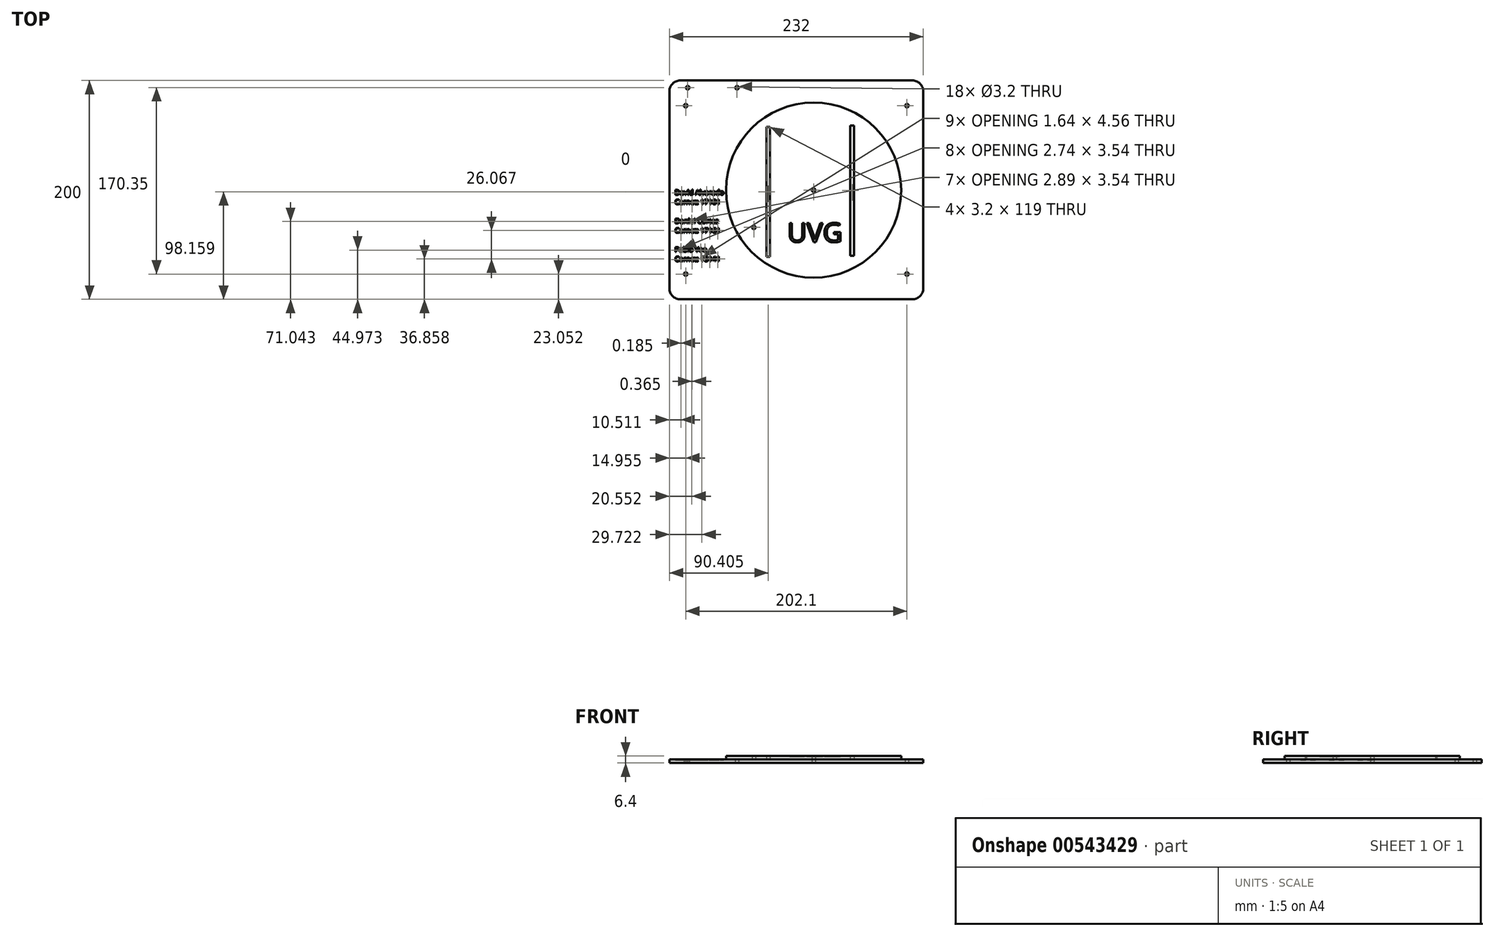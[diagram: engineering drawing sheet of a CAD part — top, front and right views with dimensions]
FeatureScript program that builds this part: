
annotation { "Feature Type Name" : "Feature", "Feature Type Description" : "" }
export const myFeature = defineFeature(function(context is Context, id is Id, definition is map)
    precondition{}
    {
        {
            var Q0;
            Q0=qCreatedBy(makeId("Top.planeOp"),FACE);
            var sketch = newSketch(context, id + "F0", { "sketchPlane" : qUnion([Q0])});
            skLineSegment(sketch, "E0.bottom", {"start": v(-92.28, 107.73) * mm, "end": v(139.72, 107.73) * mm});
            skLineSegment(sketch, "E0.top", {"start": v(-92.28, -92.27) * mm, "end": v(139.72, -92.27) * mm});
            skLineSegment(sketch, "E0.left", {"start": v(-92.28, 107.73) * mm, "end": v(-92.28, -92.27) * mm});
            skLineSegment(sketch, "E0.right", {"start": v(139.72, 107.73) * mm, "end": v(139.72, -92.27) * mm});
            skCircle(sketch, "E1", {"center": v(39.52, 7.53) * mm, "radius": 1.6 * mm});
            skCircle(sketch, "E2", {"center": v(-75.5, 101.13) * mm, "radius": 1.6 * mm});
            skCircle(sketch, "E3", {"center": v(-30.4, 101.13) * mm, "radius": 1.6 * mm});
            skCircle(sketch, "E4", {"center": v(-77.33, 84.68) * mm, "radius": 1.6 * mm});
            skCircle(sketch, "E5", {"center": v(124.77, 84.68) * mm, "radius": 1.6 * mm});
            skCircle(sketch, "E6", {"center": v(124.77, -69.22) * mm, "radius": 1.6 * mm});
            skCircle(sketch, "E7", {"center": v(-77.33, -69.22) * mm, "radius": 1.6 * mm});
            skSolve(sketch);
        }
        {
            var Q0;
            Q0=makeQuery(id+"F0.imprint","IMPRINT",FACE,{"disambiguationData":[TD([[makeQuery(id+"F0.imprint","IMPRINT",EDGE,{"derivedFrom":sQuery(id+"F0.wireOp",EDGE,"E0.bottom")}),-1.0]])]});
            extrude(context, id + "F1", {"entities" : qUnion([Q0]), "depth" : 3.2 * mm});
        }
        {
            var Q0;
            Q0=makeQuery(id+"F1.opExtrude","SWEPT_EDGE",EDGE,{"disambiguationData":[OSD([sQuery(id+"F0.wireOp",EDGE,"E0.bottom"),sQuery(id+"F0.wireOp",EDGE,"E0.right")])]});
            var Q1;
            Q1=makeQuery(id+"F1.opExtrude","SWEPT_EDGE",EDGE,{"disambiguationData":[OSD([sQuery(id+"F0.wireOp",EDGE,"E0.bottom"),sQuery(id+"F0.wireOp",EDGE,"E0.left")])]});
            var Q2;
            Q2=makeQuery(id+"F1.opExtrude","SWEPT_EDGE",EDGE,{"disambiguationData":[OSD([sQuery(id+"F0.wireOp",EDGE,"E0.top"),sQuery(id+"F0.wireOp",EDGE,"E0.right")])]});
            var Q3;
            Q3=makeQuery(id+"F1.opExtrude","SWEPT_EDGE",EDGE,{"disambiguationData":[OSD([sQuery(id+"F0.wireOp",EDGE,"E0.top"),sQuery(id+"F0.wireOp",EDGE,"E0.left")])]});
            fillet(context, id + "F2", {"entities" : qUnion([Q0, Q1, Q2, Q3]), "radius" : 10 * mm, "tangentPropagation" : true, "allowEdgeOverflow" : false});
        }
        {
            var Q0;
            Q0=makeQuery(id+"F1.opExtrude","CAP_FACE",FACE,{"disambiguationData":[OSD([sQuery(id+"F0.wireOp",EDGE,"E0.bottom"),sQuery(id+"F0.wireOp",EDGE,"E0.top"),sQuery(id+"F0.wireOp",EDGE,"E0.left"),sQuery(id+"F0.wireOp",EDGE,"E0.right"),sQuery(id+"F0.wireOp",EDGE,"E1")])],"isStart":false});
            var sketch = newSketch(context, id + "F3", { "sketchPlane" : qUnion([Q0])});
            skCircle(sketch, "E8", {"center": v(39.52, 7.53) * mm, "radius": 80 * mm});
            skCircle(sketch, "E9", {"center": v(39.52, 7.53) * mm, "radius": 1.6 * mm});
            skLineSegment(sketch, "E10.bottom", {"start": v(76.32, 66.6) * mm, "end": v(73.12, 66.6) * mm});
            skLineSegment(sketch, "E10.top", {"start": v(76.32, -52.4) * mm, "end": v(73.12, -52.4) * mm});
            skLineSegment(sketch, "E10.left", {"start": v(76.32, 66.6) * mm, "end": v(76.32, -52.4) * mm});
            skLineSegment(sketch, "E10.right", {"start": v(73.12, 66.6) * mm, "end": v(73.12, -52.4) * mm});
            skLineSegment(sketch, "E11.bottom", {"start": v(-3.48, 65.39) * mm, "end": v(-0.28, 65.39) * mm});
            skLineSegment(sketch, "E11.top", {"start": v(-3.48, -53.61) * mm, "end": v(-0.28, -53.61) * mm});
            skLineSegment(sketch, "E11.left", {"start": v(-3.48, 65.39) * mm, "end": v(-3.48, -53.61) * mm});
            skLineSegment(sketch, "E11.right", {"start": v(-0.28, 65.39) * mm, "end": v(-0.28, -53.61) * mm});
            skCircle(sketch, "E12", {"center": v(-15.08, -26.62) * mm, "radius": 1.6 * mm});
            skSolve(sketch);
        }
        {
            var Q0;
            Q0=makeQuery(id+"F3.imprint","IMPRINT",FACE,{"disambiguationData":[TD([[makeQuery(id+"F3.imprint","IMPRINT",EDGE,{"derivedFrom":sQuery(id+"F3.wireOp",EDGE,"E8")}),1.0]])]});
            var Q1;
            Q1=makeQuery(id+"F1.opExtrude","CAP_FACE",FACE,{"disambiguationData":[OSD([sQuery(id+"F0.wireOp",EDGE,"E0.bottom"),sQuery(id+"F0.wireOp",EDGE,"E0.top"),sQuery(id+"F0.wireOp",EDGE,"E0.left"),sQuery(id+"F0.wireOp",EDGE,"E0.right"),sQuery(id+"F0.wireOp",EDGE,"E1")])],"isStart":true});
            extrude(context, id + "F4", {"entities" : qUnion([Q0, Q1]), "depth" : 3.2 * mm, "offsetDistance" : 25 * mm});
        }
        {
            var Q0;
            Q0=qSketchRegion(id+"F3",true);
            extrude(context, id + "F5", {"entities" : qUnion([Q0]), "depth" : 3.2 * mm, "offsetDistance" : 25 * mm});
        }
        {
            var Q0;
            {var subQ0=sQuery(id+"F0.wireOp",EDGE,"E0.right");var subQ1=sQuery(id+"F0.wireOp",EDGE,"E3");var subQ2=sQuery(id+"F0.wireOp",EDGE,"E2");var subQ3=sQuery(id+"F0.wireOp",EDGE,"E1");var subQ4=sQuery(id+"F0.wireOp",EDGE,"E0.left");var subQ5=sQuery(id+"F0.wireOp",EDGE,"E0.top");var subQ6=sQuery(id+"F0.wireOp",EDGE,"E0.bottom");Q0=makeQuery(id+"FOxecQIyzaDJO3S_3.boolean.opBoolean","SPLIT",FACE,{"disambiguationData":[TD([makeQuery(id+"F1.opExtrude","SWEPT_FACE",FACE,{"disambiguationData":[OSD([subQ6])]})])],"derivedFrom":makeQuery(id+"F1.opExtrude","CAP_FACE",FACE,{"disambiguationData":[OSD([subQ6,subQ5,subQ4,subQ0,subQ3,subQ2,subQ1])],"isStart":false})});}
            var sketch = newSketch(context, id + "F6", { "sketchPlane" : qUnion([Q0])});
            skText(sketch, "E13", { "text": "David Alvarado\nCarnet: 17101\n\nDaniel Cortez\nCarnet: 17161\n\nPablo Yee\nCarnet: 15141", "fontName": "OpenSans-Regular.ttf"});
            const initialGuessF6  = {"E13": [-0.08728, 0.00313, 1, 0, 0.0046]};
            skSetInitialGuess(sketch, initialGuessF6);
            skSolve(sketch);
        }
        {
            var Q0;
            Q0 = qSketchRegion(id + "F6", true);
            extrude(context, id + "F7", {"entities" : qUnion([Q0]), "operationType" : NewBodyOperationType.REMOVE, "oppositeDirection" : true, "depth" : 0.5 * mm, "offsetDistance" : 25 * mm});
        }
        {
            var Q0;
            Q0=makeQuery(id+"F4.opExtrude","CAP_FACE",FACE,{"disambiguationData":[OSD([sQuery(id+"F3.wireOp",EDGE,"E8"),sQuery(id+"F3.wireOp",EDGE,"E9"),sQuery(id+"F3.wireOp",EDGE,"E10.bottom"),sQuery(id+"F3.wireOp",EDGE,"E10.top"),sQuery(id+"F3.wireOp",EDGE,"E10.left"),sQuery(id+"F3.wireOp",EDGE,"E10.right"),sQuery(id+"F3.wireOp",EDGE,"E11.bottom"),sQuery(id+"F3.wireOp",EDGE,"E11.top"),sQuery(id+"F3.wireOp",EDGE,"E11.left"),sQuery(id+"F3.wireOp",EDGE,"E11.right"),sQuery(id+"F3.wireOp",EDGE,"E12")])],"isStart":false});
            var sketch = newSketch(context, id + "F8", { "sketchPlane" : qUnion([Q0])});
            skText(sketch, "E14", { "text": "UVG", "fontName": "OpenSans-Regular.ttf"});
            const initialGuessF8  = {"E14": [0.01552, -0.04002, 1, 0, 0.01762]};
            skSetInitialGuess(sketch, initialGuessF8);
            skSolve(sketch);
        }
        {
            var Q0;
            Q0 = qSketchRegion(id + "F8", true);
            extrude(context, id + "F9", {"entities" : qUnion([Q0]), "operationType" : NewBodyOperationType.REMOVE, "oppositeDirection" : true, "depth" : 0.5 * mm, "offsetDistance" : 25 * mm});
        }
    });
